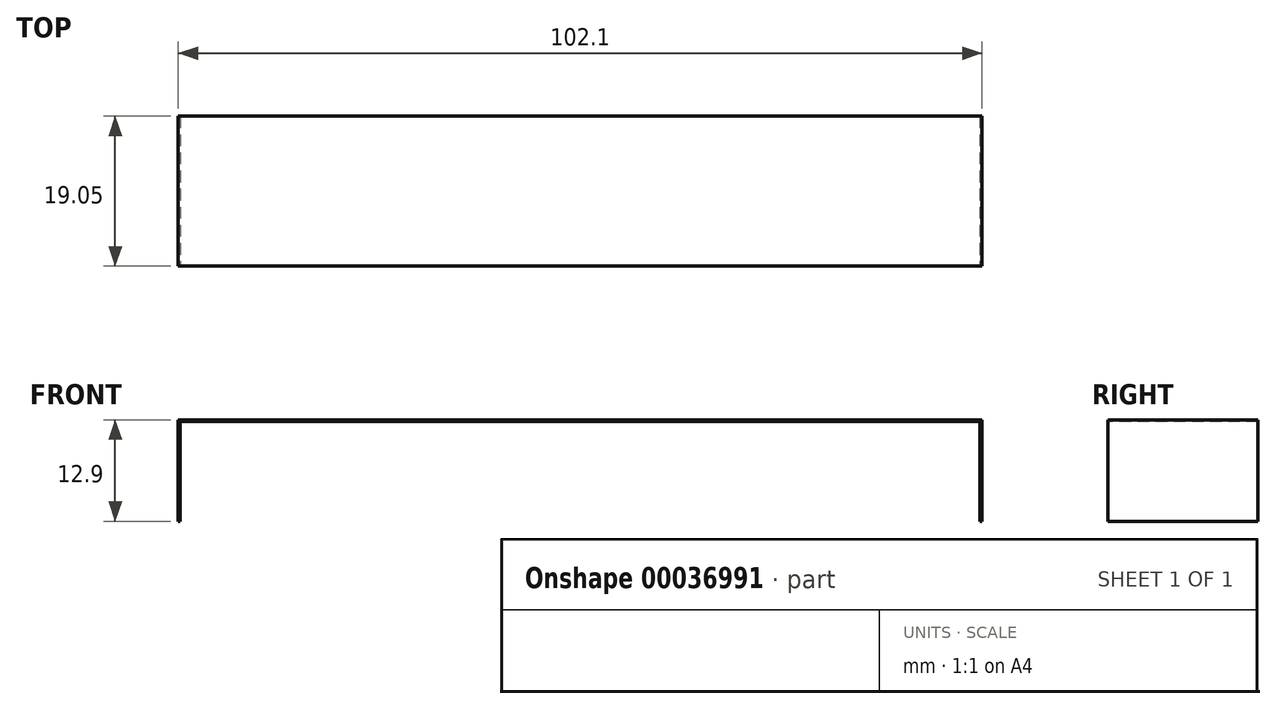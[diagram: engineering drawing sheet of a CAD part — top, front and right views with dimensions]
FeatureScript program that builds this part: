
annotation { "Feature Type Name" : "Feature", "Feature Type Description" : "" }
export const myFeature = defineFeature(function(context is Context, id is Id, definition is map)
    precondition{}
    {
        {
            var Q0;
            Q0=qCreatedBy(makeId("Top.planeOp"),FACE);
            var sketch = newSketch(context, id + "F0", { "sketchPlane" : qUnion([Q0])});
            skLineSegment(sketch, "E0.bottom", {"start": v(-51.05, 0) * mm, "end": v(51.05, 0) * mm});
            skLineSegment(sketch, "E0.top", {"start": v(-51.05, 19.05) * mm, "end": v(51.05, 19.05) * mm});
            skLineSegment(sketch, "E0.left", {"start": v(-51.05, 0) * mm, "end": v(-51.05, 19.05) * mm});
            skLineSegment(sketch, "E0.right", {"start": v(51.05, 0) * mm, "end": v(51.05, 19.05) * mm});
            skSolve(sketch);
        }
        {
            var Q0;
            Q0 = qSketchRegion(id + "F0", true);
            extrude(context, id + "F1", {"entities" : qUnion([Q0]), "depth" : 0.2 * mm});
        }
        {
            var Q0;
            Q0=makeQuery(id+"F1.opExtrude","CAP_FACE",FACE,{"disambiguationData":[OSD([sQuery(id+"F0.wireOp",EDGE,"E0.bottom"),sQuery(id+"F0.wireOp",EDGE,"E0.top"),sQuery(id+"F0.wireOp",EDGE,"E0.left"),sQuery(id+"F0.wireOp",EDGE,"E0.right")])],"isStart":true});
            var sketch = newSketch(context, id + "F2", { "sketchPlane" : qUnion([Q0])});
            skLineSegment(sketch, "E1.bottom", {"start": v(-51.05, -19.05) * mm, "end": v(-50.8, -19.05) * mm});
            skLineSegment(sketch, "E1.top", {"start": v(-51.05, 0) * mm, "end": v(-50.8, 0) * mm});
            skLineSegment(sketch, "E1.left", {"start": v(-51.05, -19.05) * mm, "end": v(-51.05, 0) * mm});
            skLineSegment(sketch, "E1.right", {"start": v(-50.8, -19.05) * mm, "end": v(-50.8, 0) * mm});
            skLineSegment(sketch, "E2", {"start": v(0, 0) * mm, "end": v(0, -19.05) * mm});
            skLineSegment(sketch, "E3.MirrorCS", {"start": v(50.8, -19.05) * mm, "end": v(50.8, 0) * mm});
            skSolve(sketch);
        }
        {
            var Q0;
            Q0 = qSketchRegion(id + "F2", true);
            var Q1;
            {var subQ0=sQuery(id+"F2.wireOp",EDGE,"E3.MirrorCS");Q1=makeQuery(id+"F2.imprint","IMPRINT",FACE,{"disambiguationData":[TD([[makeQuery(id+"F2.imprint","IMPRINT",EDGE,{"derivedFrom":subQ0}),-1.0]])]});}
            extrude(context, id + "F3", {"entities" : qUnion([Q0, Q1]), "operationType" : NewBodyOperationType.ADD, "depth" : 12.7 * mm});
        }
    });
